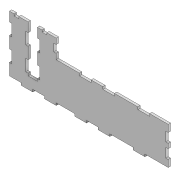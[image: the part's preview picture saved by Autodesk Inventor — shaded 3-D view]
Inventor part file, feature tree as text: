
AUTODESK INVENTOR PART (.ipt)
format: ipt  version: 2022 (Build 260153000, 153)  size: 301,568 bytes
history: native  units: mm
features: extrude x3, sketch x3, projected_geometry x2
ambient origin geometry x8: Origin, YZ Plane, XZ Plane, XY Plane, X Axis, Y Axis, Z Axis, Center Point
bodies: Solid1 (feature_tree)
feature tree (8):
  extrude  "Extrusion1"  Depth=40.0mm
  extrude  "Extrusion2"  Depth=25.0mm
  extrude  "Extrusion3"  Depth=25.0mm
  sketch  "Sketch1"  dims[d2=80.0mm d3=40.0mm]
  sketch  "Sketch2"  dims[d4=5.0mm d5=0.0mm d6=25.0mm]
  projected_geometry  "Projected Loop1"
  sketch  "Sketch3"  dims[d7=5.0mm d8=25.0mm d9=25.0mm d10=5.0mm d20=40.0mm d21=50.0mm d22=25.0mm d23=40.0mm d24=20.0mm d26=20.0mm d27=120.0mm d28=120.0mm d29=5.0mm d30=25.0mm d31=5.0mm d32=25.0mm d33=25.0mm d34=25.0mm d35=5.0mm d36=5.0mm d37=5.0mm d38=16.0mm d39=12.0mm d40=25.0mm d41=5.0mm d42=25.0mm d44=25.0mm d45=25.0mm d46=5.0mm d47=5.0mm d48=20.0mm d49=20.0mm d50=10.0mm d51=15.0mm d52=5.0mm d53=0.0mm d54=10.0mm d55=10.0mm d56=10.0mm d57=10.0mm d58=280.0mm d59=10.0mm d60=10.0mm d61=10.0mm d62=10.0mm d63=10.0mm d64=5.0mm d65=0.0mm]
  projected_geometry  "Projected Loop2"
